# Revit family: 0053897 Sylvania Lighting Fixture START eco Downlight Flat Sq 1400lm 840 DIM
name_source: partatom
category: Lighting Fixtures
revit_build: Autodesk Revit 2016 (Build: 20150220_1215(x64)
units: mm (PartAtom-declared; Revit-internal decimal feet)

## family parameters
Cut with Voids When Loaded = No
Host = Face
Light Source = Yes
OmniClass Number = 23.80.70.11.14.11
OmniClass Title = Downlights
Part Type = Normal
Room Calculation Point = No
Round Connector Dimension = Use Diameter
Shared = No

## types (1)
- 0053897 START eco Downlight Flat Sq 1400lm 840 DIM
    AccessoryMaterial = Diffuser-Sylvania-Glow
    Apparent Load = 0 VA
    Assembly Code = D5020200
    AssetType = Fixed
    BodyHeight_FEILO = 12 mm  [stored 0.0393701 ft]
    BodyLength_FEILO = 226 mm  [stored 0.74147 ft]
    BodyMaterial = Body-Sylvania-SylFlatDimmable-White
    BodyRadius = 10 mm  [stored 0.0328084 ft]
    BodyRadiusUpper = 3 mm  [stored 0.00984252 ft]
    BodyWidth_FEILO = 226 mm  [stored 0.74147 ft]
    ClassificationName = Uniclass2015
    ClassificationValue = EF_70_80
    Color Filter = 16777215
    Cost = 0 $
    CutoutHeight_FEILO = 32 mm
    Default Elevation = 1219 mm
    Description = Integrated LED recessed downlight providing 1530 fixture lumens at a wattage of 18W giving a high efficacy of 85lm/W. Fitting includes Leading/Trailing edge phase dimmable driver and has a square ceiling cut out of 206x206mm with an IP20 and IK02 rating providing uniform distribution with an Opal diffuser and 110° beam angle. Provided including a Loop in Loop out box and built Built white aluminium housing.
    DiffuserMaterial = Diffuser-Sylvania-Glow
    Dimming Lamp Color Temperature Shift = <None>
    DimmingControlOptions = Dimmable
    DocumentationLiterature = http://www.feilosylvania.com
    DurationUnit = hours
    ElectricShockClassification = Class II
    Emit Shape Visible in Rendering = No
    Emit from Rectangle Length = 178 mm  [stored 0.58399 ft]
    Emit from Rectangle Width = 178 mm  [stored 0.58399 ft]
    ExpectedLife = 50000
    IfcExportAs = IfcLightFixtureType
    IfcExportType = IfcLightFixtureType
    ImpactProtectionIndex = IK06
    IngressProtection = IP44
    InputNominalFrequency = 50/60 Hz
    InputVoltage = 220-240V~
    Keynote = 16500
    Lamp = LED
    LampColourRenderingIndex = 80
    LampColourTemperature = 4000 K
    LampNominalLuminous = 1530 lm
    LampsType = LED
    LightOutputRatio = 1
    LuminaireType = LED recessed downlight
    LuminousEfficacy = 85 lm/W
    Manufacturer = Feilo Sylvania
    ManufacturerName = Feilo Sylvania
    Material = Aluminium
    Model = START eco Downlight Flat Sq 1400lm 840 DIM
    ModelNumber = 0053897
    ModelReference = START eco Downlight Flat Sq 1400lm 840 DIM
    Name = START eco Downlight Flat Sq 1400lm 840 DIM
    NominalDepth = 226 mm  [stored 0.74147 ft]
    NominalHeight = 25 mm  [stored 0.082021 ft]
    NominalLength = 226 mm  [stored 0.74147 ft]
    Photometric Web File = 0053315.ies
    PowerConsumption = 18 W
    PowerFactor = 0
    RecessedDiameter_FEILO = 209 mm  [stored 0.685696 ft]
    RecessedHeight_FEILO = 25 mm  [stored 0.082021 ft]
    ReflectorMaterial = <By Category>
    Tilt Angle = -90.00°
    Type Image = <None>
    TypeName = START eco Downlight Flat Sq 1400lm 840 DIM
    URL = http://www.feilosylvania.com
    Voltage = 230 V
    WarrantyDurationUnit = year
    Weight = 7.97 kg

note: [stored X ft] marks values corroborated as IEEE doubles in the binary element streams (Revit-internal decimal feet)

## geometry (parser evidence)
native form markers: Sweep x3
no freeform markers — native parametric forms only
